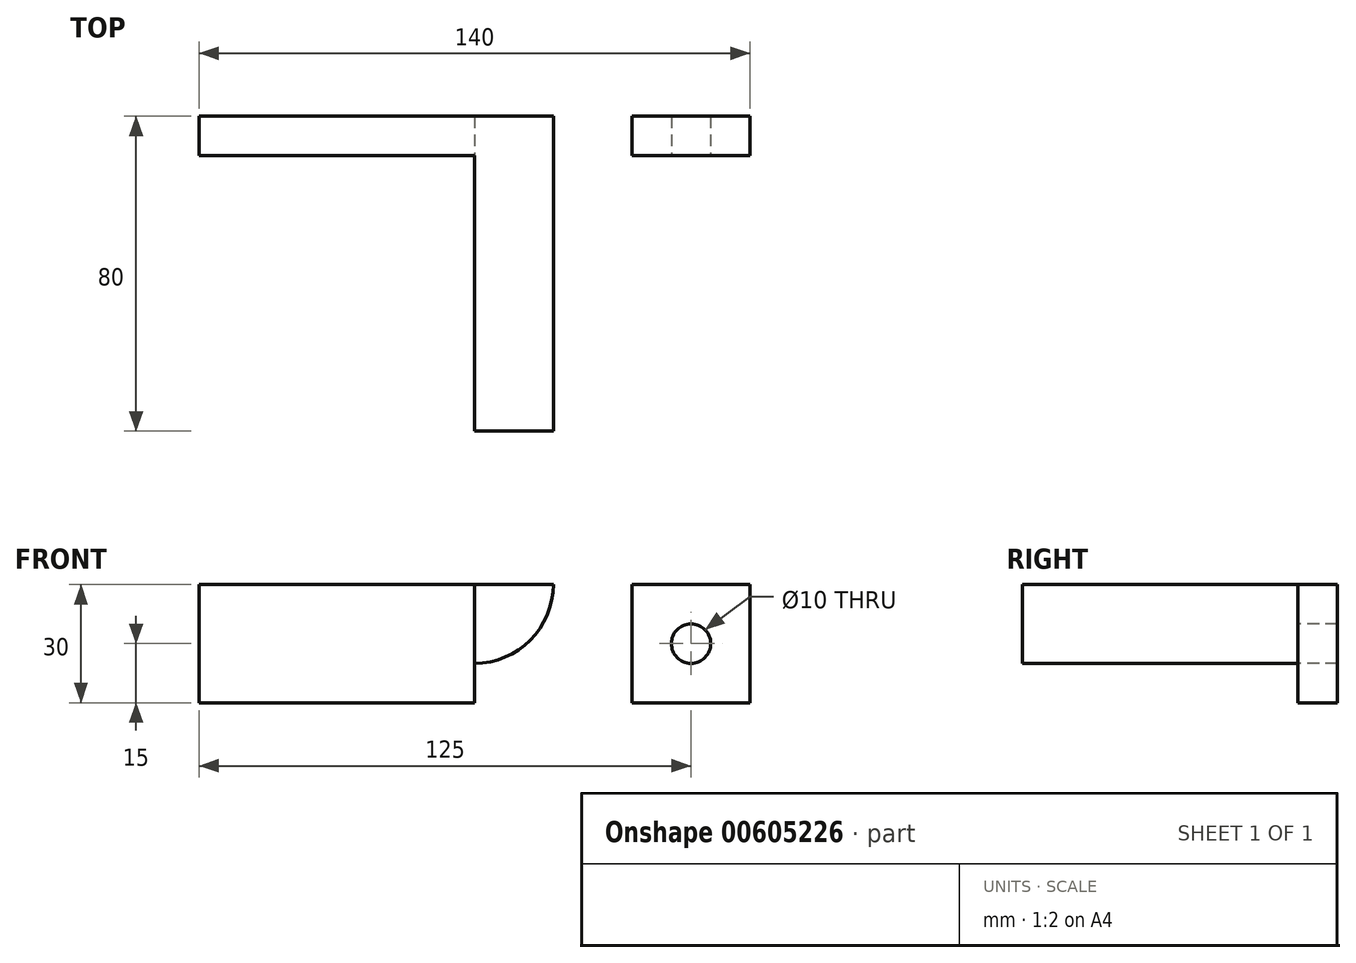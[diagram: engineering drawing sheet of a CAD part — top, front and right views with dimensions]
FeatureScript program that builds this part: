
annotation { "Feature Type Name" : "Feature", "Feature Type Description" : "" }
export const myFeature = defineFeature(function(context is Context, id is Id, definition is map)
    precondition{}
    {
        {
            var Q0;
            Q0=qCreatedBy(makeId("Right.planeOp"),FACE);
            var sketch = newSketch(context, id + "F0", { "sketchPlane" : qUnion([Q0])});
            skLineSegment(sketch, "E0", {"start": v(0, 30) * mm, "end": v(0, 0) * mm});
            skLineSegment(sketch, "E1", {"start": v(0, 0) * mm, "end": v(-60, 0) * mm});
            skLineSegment(sketch, "E2", {"start": v(-60, 0) * mm, "end": v(-60, -30) * mm});
            skLineSegment(sketch, "E3", {"start": v(-60, -30) * mm, "end": v(10, -30) * mm});
            skLineSegment(sketch, "E4", {"start": v(10, -30) * mm, "end": v(10, 30) * mm});
            skLineSegment(sketch, "E5", {"start": v(10, 30) * mm, "end": v(0, 30) * mm});
            skArc(sketch, "E6", {"start": v(-5, -30) * mm, "mid": v(-25, -10) * mm, "end": v(-45, -30) * mm});
            skSolve(sketch);
        }
        {
            var Q0;
            Q0=makeQuery(id+"F0.imprint","IMPRINT",FACE,{"disambiguationData":[TD([[makeQuery(id+"F0.imprint","IMPRINT",EDGE,{"derivedFrom":sQuery(id+"F0.wireOp",EDGE,"E0")}),1.0]])]});
            extrude(context, id + "F1", {"entities" : qUnion([Q0]), "depth" : 140 * mm, "offsetDistance" : 25 * mm, "symmetric" : true});
        }
        {
            var Q0;
            Q0=makeQuery(id+"F1.opExtrude","SWEPT_FACE",FACE,{"disambiguationData":[OSD([sQuery(id+"F0.wireOp",EDGE,"E0")])]});
            var sketch = newSketch(context, id + "F2", { "sketchPlane" : qUnion([Q0])});
            skLineSegment(sketch, "E7.bottom", {"start": v(0, 30) * mm, "end": v(40, 30) * mm});
            skLineSegment(sketch, "E7.top", {"start": v(0, 0) * mm, "end": v(40, 0) * mm});
            skLineSegment(sketch, "E7.left", {"start": v(0, 30) * mm, "end": v(0, 0) * mm});
            skLineSegment(sketch, "E7.right", {"start": v(40, 30) * mm, "end": v(40, 0) * mm});
            skSolve(sketch);
        }
        {
            var Q0;
            Q0=makeQuery(id+"F2.imprint","IMPRINT",FACE,{"disambiguationData":[TD([[makeQuery(id+"F2.imprint","IMPRINT",EDGE,{"derivedFrom":sQuery(id+"F2.wireOp",EDGE,"E7.bottom")}),1.0]])]});
            var Q1;
            Q1=makeQuery(id+"F1.opExtrude","SWEPT_FACE",FACE,{"disambiguationData":[OSD([sQuery(id+"F0.wireOp",EDGE,"E2")])]});
            extrude(context, id + "F3", {"entities" : qUnion([Q0]), "operationType" : NewBodyOperationType.ADD, "endBound" : BoundingType.UP_TO_SURFACE, "depth" : 25 * mm, "endBoundEntityFace" : qUnion([Q1]), "offsetDistance" : 25 * mm});
        }
        {
            var Q0;
            {var subQ0=sQuery(id+"F0.wireOp",EDGE,"E2");Q0=makeQuery(id+"FFP6mzLCjJNj5NH_1.1.F3.boolean.opBoolean","MERGE",FACE,{"derivedFrom":[makeQuery(id+"F3.boolean.opBoolean","MERGE",FACE,{"derivedFrom":[makeQuery(id+"F1.opExtrude","SWEPT_FACE",FACE,{"disambiguationData":[OSD([subQ0])]}),makeQuery(id+"F3.opExtrude","CAP_FACE",FACE,{"disambiguationData":[OSD([subQ0])],"isStart":false})]}),makeQuery(id+"FFP6mzLCjJNj5NH_1.1.F3.opExtrude","CAP_FACE",FACE,{"disambiguationData":[OSD([subQ0])],"isStart":false})]});}
            var sketch = newSketch(context, id + "F4", { "sketchPlane" : qUnion([Q0])});
            skArc(sketch, "E8", {"start": v(20, 30) * mm, "mid": v(0, 10) * mm, "end": v(-20, 30) * mm});
            skLineSegment(sketch, "E9", {"start": v(-20, 30) * mm, "end": v(20, 30) * mm});
            skSolve(sketch);
        }
        {
            var Q0;
            Q0=makeQuery(id+"F4.imprint","IMPRINT",FACE,{"disambiguationData":[TD([[makeQuery(id+"F4.imprint","IMPRINT",EDGE,{"derivedFrom":sQuery(id+"F4.wireOp",EDGE,"E8")}),-1.0]])]});
            extrude(context, id + "F5", {"entities" : qUnion([Q0]), "operationType" : NewBodyOperationType.REMOVE, "oppositeDirection" : true, "depth" : 129.7 * mm, "offsetDistance" : 25 * mm});
        }
        {
            var Q0;
            {var subQ0=sQuery(id+"F0.wireOp",EDGE,"E2");Q0=makeQuery(id+"FFP6mzLCjJNj5NH_1.1.F3.boolean.opBoolean","MERGE",FACE,{"derivedFrom":[makeQuery(id+"F3.boolean.opBoolean","MERGE",FACE,{"derivedFrom":[makeQuery(id+"F1.opExtrude","SWEPT_FACE",FACE,{"disambiguationData":[OSD([subQ0])]}),makeQuery(id+"F3.opExtrude","CAP_FACE",FACE,{"disambiguationData":[OSD([subQ0])],"isStart":false})]}),makeQuery(id+"FFP6mzLCjJNj5NH_1.1.F3.opExtrude","CAP_FACE",FACE,{"disambiguationData":[OSD([subQ0])],"isStart":false})]});}
            var sketch = newSketch(context, id + "F6", { "sketchPlane" : qUnion([Q0])});
            skArc(sketch, "E10.0", {"start": v(20, 30) * mm, "mid": v(0, 10) * mm, "end": v(-20, 30) * mm});
            skArc(sketch, "E11", {"start": v(30, 30) * mm, "mid": v(0, 0) * mm, "end": v(-30, 30) * mm});
            skSolve(sketch);
        }
        {
            var Q0;
            {var subQ0=sQuery(id+"F6.wireOp",EDGE,"E10.0");Q0=makeQuery(id+"F6.imprint","IMPRINT",FACE,{"disambiguationData":[TD([[makeQuery(id+"F6.imprint","IMPRINT",EDGE,{"derivedFrom":subQ0}),1.0]])]});}
            extrude(context, id + "F7", {"entities" : qUnion([Q0]), "operationType" : NewBodyOperationType.ADD, "depth" : 10 * mm, "offsetDistance" : 25 * mm});
        }
        {
            var Q0;
            {var subQ2=sQuery(id+"F0.wireOp",EDGE,"E0");Q0=makeQuery(id+"F3.boolean.opBoolean","SPLIT",FACE,{"disambiguationData":[TD([makeQuery(id+"F3.opExtrude","SWEPT_FACE",FACE,{"disambiguationData":[OSD([sQuery(id+"F2.wireOp",EDGE,"E7.right")])]})])],"derivedFrom":makeQuery(id+"F1.opExtrude","SWEPT_FACE",FACE,{"disambiguationData":[OSD([subQ2])]})});}
            var sketch = newSketch(context, id + "F8", { "sketchPlane" : qUnion([Q0])});
            skCircle(sketch, "E12", {"center": v(55, 15) * mm, "radius": 5 * mm});
            skPoint(sketch, "E13", {"position": v(55, 30) * mm});
            skPoint(sketch, "E14", {"position": v(70, 15) * mm});
            skSolve(sketch);
        }
        {
            var Q0;
            Q0=makeQuery(id+"F8.imprint","IMPRINT",FACE,{"disambiguationData":[TD([[makeQuery(id+"F8.imprint","IMPRINT",EDGE,{"derivedFrom":sQuery(id+"F8.wireOp",EDGE,"E12")}),1.0]])]});
            extrude(context, id + "F9", {"entities" : qUnion([Q0]), "operationType" : NewBodyOperationType.REMOVE, "oppositeDirection" : true, "depth" : 54.2 * mm, "offsetDistance" : 25 * mm});
        }
    });
